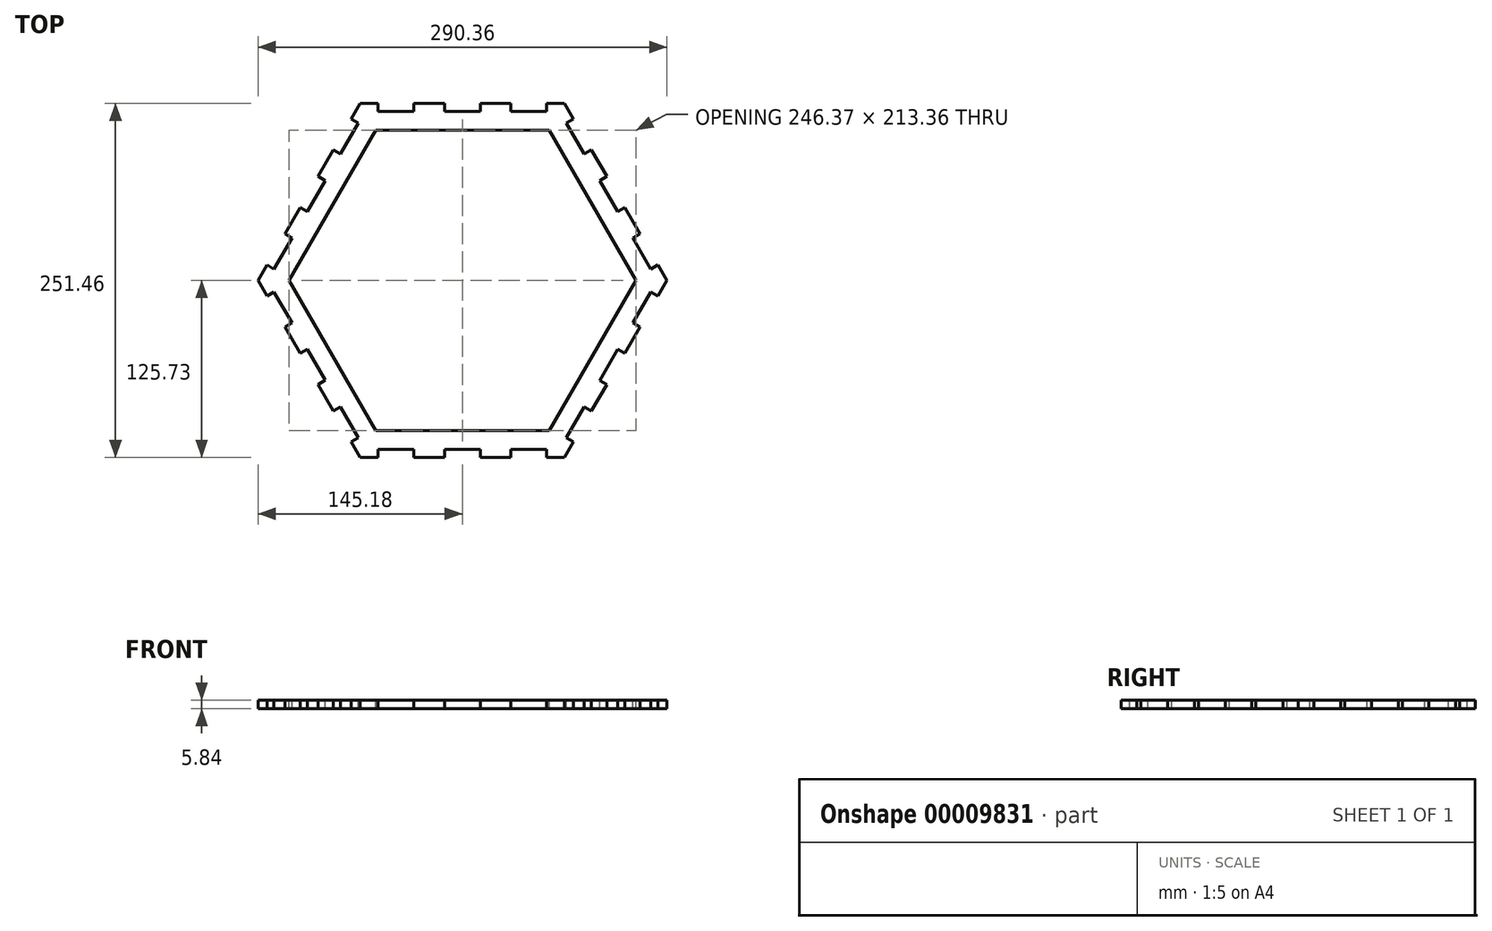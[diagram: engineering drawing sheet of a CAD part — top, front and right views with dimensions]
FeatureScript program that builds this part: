
annotation { "Feature Type Name" : "Feature", "Feature Type Description" : "" }
export const myFeature = defineFeature(function(context is Context, id is Id, definition is map)
    precondition{}
    {
        {
            var Q0;
            Q0=qCreatedBy(makeId("Top.planeOp"),FACE);
            var sketch = newSketch(context, id + "F0", { "sketchPlane" : qUnion([Q0])});
            skCircle(sketch, "E0.cCircle", {"center": v(0, 0) * mm, "radius": 125.73 * mm, "construction": true});
            skLineSegment(sketch, "E0.0", {"start": v(-72.6, 125.73) * mm, "end": v(72.6, 125.73) * mm});
            skLineSegment(sketch, "E0.1", {"start": v(72.6, 125.73) * mm, "end": v(145.18, 0) * mm});
            skLineSegment(sketch, "E0.2", {"start": v(145.18, 0) * mm, "end": v(72.6, -125.73) * mm});
            skLineSegment(sketch, "E0.3", {"start": v(72.6, -125.73) * mm, "end": v(-72.6, -125.73) * mm});
            skLineSegment(sketch, "E0.4", {"start": v(-72.6, -125.73) * mm, "end": v(-145.18, 0) * mm});
            skLineSegment(sketch, "E0.5", {"start": v(-145.18, 0) * mm, "end": v(-72.6, 125.73) * mm});
            skPoint(sketch, "E0.0.midPoint", {"position": v(0, 125.73) * mm});
            skSolve(sketch);
        }
        {
            var Q0;
            Q0=makeQuery(id+"F0.imprint","IMPRINT",FACE,{"disambiguationData":[TD([[makeQuery(id+"F0.imprint","IMPRINT",EDGE,{"derivedFrom":sQuery(id+"F0.wireOp",EDGE,"E0.0")}),-1.0]])]});
            extrude(context, id + "F1", {"entities" : qUnion([Q0]), "depth" : 5.84 * mm});
        }
        {
            var Q0;
            Q0=makeQuery(id+"F1.opExtrude","CAP_FACE",FACE,{"disambiguationData":[OSD([sQuery(id+"F0.wireOp",EDGE,"E0.0"),sQuery(id+"F0.wireOp",EDGE,"E0.1"),sQuery(id+"F0.wireOp",EDGE,"E0.2"),sQuery(id+"F0.wireOp",EDGE,"E0.3"),sQuery(id+"F0.wireOp",EDGE,"E0.4"),sQuery(id+"F0.wireOp",EDGE,"E0.5")])],"isStart":false});
            var sketch = newSketch(context, id + "F2", { "sketchPlane" : qUnion([Q0])});
            skCircle(sketch, "E1.cCircle", {"center": v(0, 0) * mm, "radius": 106.68 * mm, "construction": true});
            skLineSegment(sketch, "E1.0", {"start": v(-61.6, 106.68) * mm, "end": v(61.6, 106.68) * mm});
            skLineSegment(sketch, "E1.1", {"start": v(61.6, 106.68) * mm, "end": v(123.18, 0) * mm});
            skLineSegment(sketch, "E1.2", {"start": v(123.18, 0) * mm, "end": v(61.6, -106.68) * mm});
            skLineSegment(sketch, "E1.3", {"start": v(61.6, -106.68) * mm, "end": v(-61.6, -106.68) * mm});
            skLineSegment(sketch, "E1.4", {"start": v(-61.6, -106.68) * mm, "end": v(-123.18, 0) * mm});
            skLineSegment(sketch, "E1.5", {"start": v(-123.18, 0) * mm, "end": v(-61.6, 106.68) * mm});
            skPoint(sketch, "E1.0.midPoint", {"position": v(0, 106.68) * mm});
            skLineSegment(sketch, "E2.bottom", {"start": v(-59.9, -125.73) * mm, "end": v(-34.5, -125.73) * mm});
            skLineSegment(sketch, "E2.top", {"start": v(-59.9, -119.89) * mm, "end": v(-34.5, -119.89) * mm});
            skLineSegment(sketch, "E2.left", {"start": v(-59.9, -125.73) * mm, "end": v(-59.9, -119.89) * mm});
            skLineSegment(sketch, "E2.right", {"start": v(-34.5, -125.73) * mm, "end": v(-34.5, -119.89) * mm});
            skLineSegment(sketch, "E3.bottom", {"start": v(-12.7, -125.73) * mm, "end": v(12.7, -125.73) * mm});
            skLineSegment(sketch, "E3.top", {"start": v(-12.7, -119.89) * mm, "end": v(12.7, -119.89) * mm});
            skLineSegment(sketch, "E3.left", {"start": v(-12.7, -125.73) * mm, "end": v(-12.7, -119.89) * mm});
            skLineSegment(sketch, "E3.right", {"start": v(12.7, -125.73) * mm, "end": v(12.7, -119.89) * mm});
            skLineSegment(sketch, "E4.bottom", {"start": v(34.5, -125.73) * mm, "end": v(59.9, -125.73) * mm});
            skLineSegment(sketch, "E4.top", {"start": v(34.5, -119.89) * mm, "end": v(59.9, -119.89) * mm});
            skLineSegment(sketch, "E4.left", {"start": v(34.5, -125.73) * mm, "end": v(34.5, -119.89) * mm});
            skLineSegment(sketch, "E4.right", {"start": v(59.9, -125.73) * mm, "end": v(59.9, -119.89) * mm});
            skPoint(sketch, "E5", {"position": v(0, -119.89) * mm});
            skLineSegment(sketch, "E6.1.0", {"start": v(102.53, -73.87) * mm, "end": v(97.47, -70.95) * mm});
            skLineSegment(sketch, "E6.1.1", {"start": v(97.47, -70.95) * mm, "end": v(110.17, -48.95) * mm});
            skLineSegment(sketch, "E6.1.2", {"start": v(102.53, -73.87) * mm, "end": v(115.23, -51.87) * mm});
            skLineSegment(sketch, "E6.1.3", {"start": v(115.23, -51.87) * mm, "end": v(110.17, -48.95) * mm});
            skLineSegment(sketch, "E6.1.4", {"start": v(78.94, -114.73) * mm, "end": v(73.88, -111.81) * mm});
            skLineSegment(sketch, "E6.1.5", {"start": v(73.88, -111.81) * mm, "end": v(86.58, -89.81) * mm});
            skLineSegment(sketch, "E6.1.6", {"start": v(78.94, -114.73) * mm, "end": v(91.64, -92.73) * mm});
            skLineSegment(sketch, "E6.1.7", {"start": v(91.64, -92.73) * mm, "end": v(86.58, -89.81) * mm});
            skLineSegment(sketch, "E6.1.8", {"start": v(121.07, -30.07) * mm, "end": v(133.77, -8.08) * mm});
            skLineSegment(sketch, "E6.1.9", {"start": v(138.83, -11) * mm, "end": v(133.77, -8.08) * mm});
            skLineSegment(sketch, "E6.1.10", {"start": v(126.13, -33) * mm, "end": v(138.83, -11) * mm});
            skLineSegment(sketch, "E6.1.11", {"start": v(126.13, -33) * mm, "end": v(121.07, -30.07) * mm});
            skLineSegment(sketch, "E6.2.0", {"start": v(115.24, 51.86) * mm, "end": v(110.18, 48.94) * mm});
            skLineSegment(sketch, "E6.2.1", {"start": v(110.18, 48.94) * mm, "end": v(97.48, 70.94) * mm});
            skLineSegment(sketch, "E6.2.2", {"start": v(115.24, 51.86) * mm, "end": v(102.54, 73.86) * mm});
            skLineSegment(sketch, "E6.2.3", {"start": v(102.54, 73.86) * mm, "end": v(97.48, 70.94) * mm});
            skLineSegment(sketch, "E6.2.4", {"start": v(138.83, 11) * mm, "end": v(133.77, 8.08) * mm});
            skLineSegment(sketch, "E6.2.5", {"start": v(133.77, 8.08) * mm, "end": v(121.07, 30.07) * mm});
            skLineSegment(sketch, "E6.2.6", {"start": v(138.83, 11) * mm, "end": v(126.13, 33) * mm});
            skLineSegment(sketch, "E6.2.7", {"start": v(126.13, 33) * mm, "end": v(121.07, 30.07) * mm});
            skLineSegment(sketch, "E6.2.8", {"start": v(86.58, 89.81) * mm, "end": v(73.88, 111.81) * mm});
            skLineSegment(sketch, "E6.2.9", {"start": v(78.94, 114.73) * mm, "end": v(73.88, 111.81) * mm});
            skLineSegment(sketch, "E6.2.10", {"start": v(91.64, 92.73) * mm, "end": v(78.94, 114.73) * mm});
            skLineSegment(sketch, "E6.2.11", {"start": v(91.64, 92.73) * mm, "end": v(86.58, 89.81) * mm});
            skLineSegment(sketch, "E6.3.0", {"start": v(12.7, 125.73) * mm, "end": v(12.7, 119.89) * mm});
            skLineSegment(sketch, "E6.3.1", {"start": v(12.7, 119.89) * mm, "end": v(-12.7, 119.89) * mm});
            skLineSegment(sketch, "E6.3.2", {"start": v(12.7, 125.73) * mm, "end": v(-12.7, 125.73) * mm});
            skLineSegment(sketch, "E6.3.3", {"start": v(-12.7, 125.73) * mm, "end": v(-12.7, 119.89) * mm});
            skLineSegment(sketch, "E6.3.4", {"start": v(59.9, 125.73) * mm, "end": v(59.9, 119.89) * mm});
            skLineSegment(sketch, "E6.3.5", {"start": v(59.9, 119.89) * mm, "end": v(34.5, 119.89) * mm});
            skLineSegment(sketch, "E6.3.6", {"start": v(59.9, 125.73) * mm, "end": v(34.5, 125.73) * mm});
            skLineSegment(sketch, "E6.3.7", {"start": v(34.5, 125.73) * mm, "end": v(34.5, 119.89) * mm});
            skLineSegment(sketch, "E6.3.8", {"start": v(-34.5, 119.89) * mm, "end": v(-59.9, 119.89) * mm});
            skLineSegment(sketch, "E6.3.9", {"start": v(-59.9, 125.73) * mm, "end": v(-59.9, 119.89) * mm});
            skLineSegment(sketch, "E6.3.10", {"start": v(-34.5, 125.73) * mm, "end": v(-59.9, 125.73) * mm});
            skLineSegment(sketch, "E6.3.11", {"start": v(-34.5, 125.73) * mm, "end": v(-34.5, 119.89) * mm});
            skLineSegment(sketch, "E6.4.0", {"start": v(-102.53, 73.87) * mm, "end": v(-97.47, 70.95) * mm});
            skLineSegment(sketch, "E6.4.1", {"start": v(-97.47, 70.95) * mm, "end": v(-110.17, 48.95) * mm});
            skLineSegment(sketch, "E6.4.2", {"start": v(-102.53, 73.87) * mm, "end": v(-115.23, 51.87) * mm});
            skLineSegment(sketch, "E6.4.3", {"start": v(-115.23, 51.87) * mm, "end": v(-110.17, 48.95) * mm});
            skLineSegment(sketch, "E6.4.4", {"start": v(-78.94, 114.73) * mm, "end": v(-73.88, 111.81) * mm});
            skLineSegment(sketch, "E6.4.5", {"start": v(-73.88, 111.81) * mm, "end": v(-86.58, 89.81) * mm});
            skLineSegment(sketch, "E6.4.6", {"start": v(-78.94, 114.73) * mm, "end": v(-91.64, 92.73) * mm});
            skLineSegment(sketch, "E6.4.7", {"start": v(-91.64, 92.73) * mm, "end": v(-86.58, 89.81) * mm});
            skLineSegment(sketch, "E6.4.8", {"start": v(-121.07, 30.07) * mm, "end": v(-133.77, 8.08) * mm});
            skLineSegment(sketch, "E6.4.9", {"start": v(-138.83, 11) * mm, "end": v(-133.77, 8.08) * mm});
            skLineSegment(sketch, "E6.4.10", {"start": v(-126.13, 33) * mm, "end": v(-138.83, 11) * mm});
            skLineSegment(sketch, "E6.4.11", {"start": v(-126.13, 33) * mm, "end": v(-121.07, 30.07) * mm});
            skLineSegment(sketch, "E6.5.0", {"start": v(-115.24, -51.86) * mm, "end": v(-110.18, -48.94) * mm});
            skLineSegment(sketch, "E6.5.1", {"start": v(-110.18, -48.94) * mm, "end": v(-97.48, -70.94) * mm});
            skLineSegment(sketch, "E6.5.2", {"start": v(-115.24, -51.86) * mm, "end": v(-102.54, -73.86) * mm});
            skLineSegment(sketch, "E6.5.3", {"start": v(-102.54, -73.86) * mm, "end": v(-97.48, -70.94) * mm});
            skLineSegment(sketch, "E6.5.4", {"start": v(-138.83, -11) * mm, "end": v(-133.77, -8.08) * mm});
            skLineSegment(sketch, "E6.5.5", {"start": v(-133.77, -8.08) * mm, "end": v(-121.07, -30.07) * mm});
            skLineSegment(sketch, "E6.5.6", {"start": v(-138.83, -11) * mm, "end": v(-126.13, -33) * mm});
            skLineSegment(sketch, "E6.5.7", {"start": v(-126.13, -33) * mm, "end": v(-121.07, -30.07) * mm});
            skLineSegment(sketch, "E6.5.8", {"start": v(-86.58, -89.81) * mm, "end": v(-73.88, -111.81) * mm});
            skLineSegment(sketch, "E6.5.9", {"start": v(-78.94, -114.73) * mm, "end": v(-73.88, -111.81) * mm});
            skLineSegment(sketch, "E6.5.10", {"start": v(-91.64, -92.73) * mm, "end": v(-78.94, -114.73) * mm});
            skLineSegment(sketch, "E6.5.11", {"start": v(-91.64, -92.73) * mm, "end": v(-86.58, -89.81) * mm});
            skSolve(sketch);
        }
        {
            var Q0;
            Q0=makeQuery(id+"F2.imprint","IMPRINT",FACE,{"disambiguationData":[TD([[makeQuery(id+"F2.imprint","IMPRINT",EDGE,{"derivedFrom":sQuery(id+"F2.wireOp",EDGE,"E6.3.8")}),-1.0]])]});
            var Q1;
            Q1=makeQuery(id+"F2.imprint","IMPRINT",FACE,{"disambiguationData":[TD([[makeQuery(id+"F2.imprint","IMPRINT",EDGE,{"derivedFrom":sQuery(id+"F2.wireOp",EDGE,"E6.3.0")}),-1.0]])]});
            var Q2;
            Q2=makeQuery(id+"F2.imprint","IMPRINT",FACE,{"disambiguationData":[TD([[makeQuery(id+"F2.imprint","IMPRINT",EDGE,{"derivedFrom":sQuery(id+"F2.wireOp",EDGE,"E6.3.4")}),-1.0]])]});
            var Q3;
            Q3=makeQuery(id+"F2.imprint","IMPRINT",FACE,{"disambiguationData":[TD([[makeQuery(id+"F2.imprint","IMPRINT",EDGE,{"derivedFrom":sQuery(id+"F2.wireOp",EDGE,"E1.0")}),-1.0]])]});
            var Q4;
            Q4=makeQuery(id+"F2.imprint","IMPRINT",FACE,{"disambiguationData":[TD([[makeQuery(id+"F2.imprint","IMPRINT",EDGE,{"derivedFrom":sQuery(id+"F2.wireOp",EDGE,"E6.2.8")}),-1.0]])]});
            var Q5;
            Q5=makeQuery(id+"F2.imprint","IMPRINT",FACE,{"disambiguationData":[TD([[makeQuery(id+"F2.imprint","IMPRINT",EDGE,{"derivedFrom":sQuery(id+"F2.wireOp",EDGE,"E6.2.0")}),-1.0]])]});
            var Q6;
            Q6=makeQuery(id+"F2.imprint","IMPRINT",FACE,{"disambiguationData":[TD([[makeQuery(id+"F2.imprint","IMPRINT",EDGE,{"derivedFrom":sQuery(id+"F2.wireOp",EDGE,"E6.2.4")}),-1.0]])]});
            var Q7;
            Q7=makeQuery(id+"F2.imprint","IMPRINT",FACE,{"disambiguationData":[TD([[makeQuery(id+"F2.imprint","IMPRINT",EDGE,{"derivedFrom":sQuery(id+"F2.wireOp",EDGE,"E6.1.0")}),-1.0]])]});
            var Q8;
            Q8=makeQuery(id+"F2.imprint","IMPRINT",FACE,{"disambiguationData":[TD([[makeQuery(id+"F2.imprint","IMPRINT",EDGE,{"derivedFrom":sQuery(id+"F2.wireOp",EDGE,"E6.1.4")}),-1.0]])]});
            var Q9;
            Q9=makeQuery(id+"F2.imprint","IMPRINT",FACE,{"disambiguationData":[TD([[makeQuery(id+"F2.imprint","IMPRINT",EDGE,{"derivedFrom":sQuery(id+"F2.wireOp",EDGE,"E6.1.8")}),-1.0]])]});
            var Q10;
            Q10=makeQuery(id+"F2.imprint","IMPRINT",FACE,{"disambiguationData":[TD([[makeQuery(id+"F2.imprint","IMPRINT",EDGE,{"derivedFrom":sQuery(id+"F2.wireOp",EDGE,"E2.bottom")}),-1.0]])]});
            var Q11;
            Q11=makeQuery(id+"F2.imprint","IMPRINT",FACE,{"disambiguationData":[TD([[makeQuery(id+"F2.imprint","IMPRINT",EDGE,{"derivedFrom":sQuery(id+"F2.wireOp",EDGE,"E3.bottom")}),-1.0]])]});
            var Q12;
            Q12=makeQuery(id+"F2.imprint","IMPRINT",FACE,{"disambiguationData":[TD([[makeQuery(id+"F2.imprint","IMPRINT",EDGE,{"derivedFrom":sQuery(id+"F2.wireOp",EDGE,"E4.bottom")}),-1.0]])]});
            var Q13;
            Q13=makeQuery(id+"F2.imprint","IMPRINT",FACE,{"disambiguationData":[TD([[makeQuery(id+"F2.imprint","IMPRINT",EDGE,{"derivedFrom":sQuery(id+"F2.wireOp",EDGE,"E6.5.8")}),-1.0]])]});
            var Q14;
            Q14=makeQuery(id+"F2.imprint","IMPRINT",FACE,{"disambiguationData":[TD([[makeQuery(id+"F2.imprint","IMPRINT",EDGE,{"derivedFrom":sQuery(id+"F2.wireOp",EDGE,"E6.5.0")}),-1.0]])]});
            var Q15;
            Q15=makeQuery(id+"F2.imprint","IMPRINT",FACE,{"disambiguationData":[TD([[makeQuery(id+"F2.imprint","IMPRINT",EDGE,{"derivedFrom":sQuery(id+"F2.wireOp",EDGE,"E6.5.4")}),-1.0]])]});
            var Q16;
            Q16=makeQuery(id+"F2.imprint","IMPRINT",FACE,{"disambiguationData":[TD([[makeQuery(id+"F2.imprint","IMPRINT",EDGE,{"derivedFrom":sQuery(id+"F2.wireOp",EDGE,"E6.4.8")}),-1.0]])]});
            var Q17;
            Q17=makeQuery(id+"F2.imprint","IMPRINT",FACE,{"disambiguationData":[TD([[makeQuery(id+"F2.imprint","IMPRINT",EDGE,{"derivedFrom":sQuery(id+"F2.wireOp",EDGE,"E6.4.0")}),-1.0]])]});
            var Q18;
            Q18=makeQuery(id+"F2.imprint","IMPRINT",FACE,{"disambiguationData":[TD([[makeQuery(id+"F2.imprint","IMPRINT",EDGE,{"derivedFrom":sQuery(id+"F2.wireOp",EDGE,"E6.4.4")}),-1.0]])]});
            var Q19;
            Q19=makeQuery(id+"F2.imprint","IMPRINT",FACE,{"disambiguationData":[TD([[makeQuery(id+"F2.imprint","IMPRINT",EDGE,{"derivedFrom":sQuery(id+"F2.wireOp",EDGE,"4ddb2eb4-8a15-486a-b36b-cabe7433b5ea.4.2")}),1.0]])]});
            var Q20;
            Q20=makeQuery(id+"F2.imprint","IMPRINT",FACE,{"disambiguationData":[TD([[makeQuery(id+"F2.imprint","IMPRINT",EDGE,{"derivedFrom":sQuery(id+"F2.wireOp",EDGE,"4ddb2eb4-8a15-486a-b36b-cabe7433b5ea.4.5")}),-1.0]])]});
            var Q21;
            Q21=makeQuery(id+"F2.imprint","IMPRINT",FACE,{"disambiguationData":[TD([[makeQuery(id+"F2.imprint","IMPRINT",EDGE,{"derivedFrom":sQuery(id+"F2.wireOp",EDGE,"4ddb2eb4-8a15-486a-b36b-cabe7433b5ea.4.8")}),-1.0]])]});
            var Q22;
            Q22=makeQuery(id+"F2.imprint","IMPRINT",FACE,{"disambiguationData":[TD([[makeQuery(id+"F2.imprint","IMPRINT",EDGE,{"derivedFrom":sQuery(id+"F2.wireOp",EDGE,"4ddb2eb4-8a15-486a-b36b-cabe7433b5ea.3.10")}),1.0]])]});
            var Q23;
            Q23=makeQuery(id+"F2.imprint","IMPRINT",FACE,{"disambiguationData":[TD([[makeQuery(id+"F2.imprint","IMPRINT",EDGE,{"derivedFrom":sQuery(id+"F2.wireOp",EDGE,"4ddb2eb4-8a15-486a-b36b-cabe7433b5ea.3.1")}),-1.0]])]});
            var Q24;
            Q24=makeQuery(id+"F2.imprint","IMPRINT",FACE,{"disambiguationData":[TD([[makeQuery(id+"F2.imprint","IMPRINT",EDGE,{"derivedFrom":sQuery(id+"F2.wireOp",EDGE,"4ddb2eb4-8a15-486a-b36b-cabe7433b5ea.3.5")}),-1.0]])]});
            var Q25;
            Q25=makeQuery(id+"F2.imprint","IMPRINT",FACE,{"disambiguationData":[TD([[makeQuery(id+"F2.imprint","IMPRINT",EDGE,{"derivedFrom":sQuery(id+"F2.wireOp",EDGE,"4ddb2eb4-8a15-486a-b36b-cabe7433b5ea.2.10")}),1.0]])]});
            var Q26;
            Q26=makeQuery(id+"F2.imprint","IMPRINT",FACE,{"disambiguationData":[TD([[makeQuery(id+"F2.imprint","IMPRINT",EDGE,{"derivedFrom":sQuery(id+"F2.wireOp",EDGE,"4ddb2eb4-8a15-486a-b36b-cabe7433b5ea.2.1")}),-1.0]])]});
            var Q27;
            Q27=makeQuery(id+"F2.imprint","IMPRINT",FACE,{"disambiguationData":[TD([[makeQuery(id+"F2.imprint","IMPRINT",EDGE,{"derivedFrom":sQuery(id+"F2.wireOp",EDGE,"4ddb2eb4-8a15-486a-b36b-cabe7433b5ea.2.6")}),1.0]])]});
            var Q28;
            Q28=makeQuery(id+"F2.imprint","IMPRINT",FACE,{"disambiguationData":[TD([[makeQuery(id+"F2.imprint","IMPRINT",EDGE,{"derivedFrom":sQuery(id+"F2.wireOp",EDGE,"4ddb2eb4-8a15-486a-b36b-cabe7433b5ea.1.8")}),-1.0]])]});
            var Q29;
            Q29=makeQuery(id+"F2.imprint","IMPRINT",FACE,{"disambiguationData":[TD([[makeQuery(id+"F2.imprint","IMPRINT",EDGE,{"derivedFrom":sQuery(id+"F2.wireOp",EDGE,"4ddb2eb4-8a15-486a-b36b-cabe7433b5ea.1.2")}),1.0]])]});
            var Q30;
            Q30=makeQuery(id+"F2.imprint","IMPRINT",FACE,{"disambiguationData":[TD([[makeQuery(id+"F2.imprint","IMPRINT",EDGE,{"derivedFrom":sQuery(id+"F2.wireOp",EDGE,"4ddb2eb4-8a15-486a-b36b-cabe7433b5ea.1.6")}),1.0]])]});
            var Q31;
            Q31=makeQuery(id+"F2.imprint","IMPRINT",FACE,{"disambiguationData":[TD([[makeQuery(id+"F2.imprint","IMPRINT",EDGE,{"derivedFrom":sQuery(id+"F2.wireOp",EDGE,"055d75b2-3d57-44e9-8f90-68ccc02bbce1.bottom")}),1.0]])]});
            var Q32;
            Q32=makeQuery(id+"F2.imprint","IMPRINT",FACE,{"disambiguationData":[TD([[makeQuery(id+"F2.imprint","IMPRINT",EDGE,{"derivedFrom":sQuery(id+"F2.wireOp",EDGE,"739c4818-5ea8-4f3c-8bca-86b5378ee93f.bottom")}),1.0]])]});
            var Q33;
            Q33=makeQuery(id+"F2.imprint","IMPRINT",FACE,{"disambiguationData":[TD([[makeQuery(id+"F2.imprint","IMPRINT",EDGE,{"derivedFrom":sQuery(id+"F2.wireOp",EDGE,"d1e8aee7-1bfb-485d-87c9-a29fd40470bb.top")}),-1.0]])]});
            var Q34;
            Q34=makeQuery(id+"F2.imprint","IMPRINT",FACE,{"disambiguationData":[TD([[makeQuery(id+"F2.imprint","IMPRINT",EDGE,{"derivedFrom":sQuery(id+"F2.wireOp",EDGE,"4ddb2eb4-8a15-486a-b36b-cabe7433b5ea.5.10")}),1.0]])]});
            var Q35;
            Q35=makeQuery(id+"F2.imprint","IMPRINT",FACE,{"disambiguationData":[TD([[makeQuery(id+"F2.imprint","IMPRINT",EDGE,{"derivedFrom":sQuery(id+"F2.wireOp",EDGE,"4ddb2eb4-8a15-486a-b36b-cabe7433b5ea.5.2")}),1.0]])]});
            var Q36;
            Q36=makeQuery(id+"F2.imprint","IMPRINT",FACE,{"disambiguationData":[TD([[makeQuery(id+"F2.imprint","IMPRINT",EDGE,{"derivedFrom":sQuery(id+"F2.wireOp",EDGE,"4ddb2eb4-8a15-486a-b36b-cabe7433b5ea.5.6")}),1.0]])]});
            var Q37;
            Q37=makeQuery(id+"F2.imprint","IMPRINT",FACE,{"disambiguationData":[TD([[makeQuery(id+"F2.imprint","IMPRINT",EDGE,{"derivedFrom":sQuery(id+"F2.wireOp",EDGE,"a1ae4c75-8099-45db-a9de-46c6db8b6d34.5")}),-1.0]])]});
            extrude(context, id + "F3", {"entities" : qUnion([Q0, Q1, Q2, Q3, Q4, Q5, Q6, Q7, Q8, Q9, Q10, Q11, Q12, Q13, Q14, Q15, Q16, Q17, Q18, Q19, Q20, Q21, Q22, Q23, Q24, Q25, Q26, Q27, Q28, Q29, Q30, Q31, Q32, Q33, Q34, Q35, Q36, Q37]), "operationType" : NewBodyOperationType.REMOVE, "oppositeDirection" : true, "depth" : 25.4 * mm});
        }
    });
